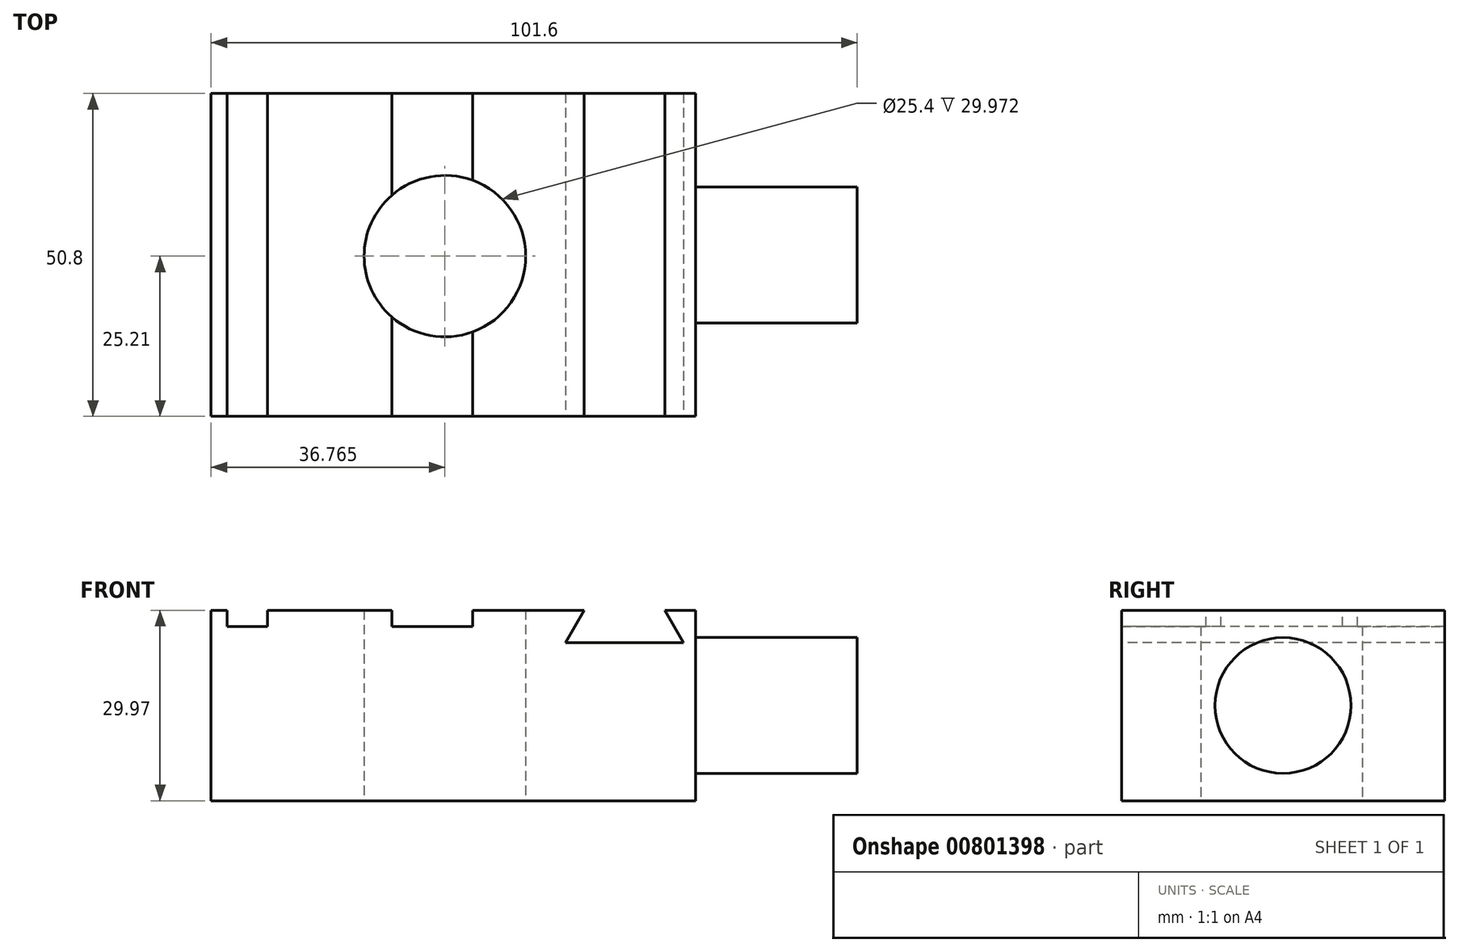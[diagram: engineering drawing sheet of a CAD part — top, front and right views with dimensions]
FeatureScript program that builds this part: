
annotation { "Feature Type Name" : "Feature", "Feature Type Description" : "" }
export const myFeature = defineFeature(function(context is Context, id is Id, definition is map)
    precondition{}
    {
        {
            var Q0;
            Q0=qCreatedBy(makeId("Top.planeOp"),FACE);
            var sketch = newSketch(context, id + "F0", { "sketchPlane" : qUnion([Q0])});
            skLineSegment(sketch, "E0.bottom", {"start": v(-34.76, 25.6) * mm, "end": v(41.44, 25.6) * mm});
            skLineSegment(sketch, "E0.top", {"start": v(-34.76, -25.2) * mm, "end": v(41.44, -25.2) * mm});
            skLineSegment(sketch, "E0.left", {"start": v(-34.76, 25.6) * mm, "end": v(-34.76, -25.2) * mm});
            skLineSegment(sketch, "E0.right", {"start": v(41.44, 25.6) * mm, "end": v(41.44, -25.2) * mm});
            skCircle(sketch, "E1", {"center": v(2, 0) * mm, "radius": 12.7 * mm});
            skSolve(sketch);
        }
        {
            var Q0;
            Q0=makeQuery(id+"F0.imprint","IMPRINT",FACE,{"disambiguationData":[TD([[makeQuery(id+"F0.imprint","IMPRINT",EDGE,{"derivedFrom":sQuery(id+"F0.wireOp",EDGE,"E0.bottom")}),-1.0]])]});
            extrude(context, id + "F1", {"entities" : qUnion([Q0]), "depth" : 29.97 * mm, "offsetDistance" : 25.4 * mm});
        }
        {
            var Q0;
            Q0=makeQuery(id+"F1.opExtrude","CAP_FACE",FACE,{"disambiguationData":[OSD([sQuery(id+"F0.wireOp",EDGE,"E0.bottom"),sQuery(id+"F0.wireOp",EDGE,"E0.top"),sQuery(id+"F0.wireOp",EDGE,"E0.left"),sQuery(id+"F0.wireOp",EDGE,"E0.right"),sQuery(id+"F0.wireOp",EDGE,"E1")])],"isStart":false});
            var sketch = newSketch(context, id + "F2", { "sketchPlane" : qUnion([Q0])});
            skLineSegment(sketch, "E2.bottom", {"start": v(-32.22, 25.6) * mm, "end": v(-25.87, 25.6) * mm});
            skLineSegment(sketch, "E2.top", {"start": v(-32.22, -25.2) * mm, "end": v(-25.87, -25.2) * mm});
            skLineSegment(sketch, "E2.left", {"start": v(-32.22, 25.6) * mm, "end": v(-32.22, -25.2) * mm});
            skLineSegment(sketch, "E2.right", {"start": v(-25.87, 25.6) * mm, "end": v(-25.87, -25.2) * mm});
            skLineSegment(sketch, "E3", {"start": v(-6.35, 25.6) * mm, "end": v(-6.35, -25.2) * mm});
            skLineSegment(sketch, "E4", {"start": v(-6.35, -25.2) * mm, "end": v(6.35, -25.2) * mm});
            skLineSegment(sketch, "E5", {"start": v(6.35, -25.2) * mm, "end": v(6.35, 25.6) * mm});
            skLineSegment(sketch, "E6", {"start": v(6.35, 25.6) * mm, "end": v(-6.35, 25.6) * mm});
            skPoint(sketch, "E7", {"position": v(0, 0) * mm});
            skLineSegment(sketch, "E8", {"start": v(0, 25.6) * mm, "end": v(0, -25.2) * mm, "construction": true});
            skSolve(sketch);
        }
        {
            var Q0;
            Q0=makeQuery(id+"F2.imprint","IMPRINT",FACE,{"disambiguationData":[TD([[makeQuery(id+"F2.imprint","IMPRINT",EDGE,{"derivedFrom":sQuery(id+"F2.wireOp",EDGE,"E2.bottom")}),-1.0]])]});
            var Q1;
            {var subQ0=sQuery(id+"F2.wireOp",EDGE,"E6");Q1=makeQuery(id+"F2.imprint","IMPRINT",FACE,{"disambiguationData":[TD([[makeQuery(id+"F2.imprint","IMPRINT",EDGE,{"derivedFrom":subQ0}),-1.0]])]});}
            var Q2;
            {var subQ0=sQuery(id+"F2.wireOp",EDGE,"E4");Q2=makeQuery(id+"F2.imprint","IMPRINT",FACE,{"disambiguationData":[TD([[makeQuery(id+"F2.imprint","IMPRINT",EDGE,{"derivedFrom":subQ0}),1.0]])]});}
            extrude(context, id + "F3", {"entities" : qUnion([Q0, Q1, Q2]), "operationType" : NewBodyOperationType.REMOVE, "oppositeDirection" : true, "depth" : 2.54 * mm, "offsetDistance" : 25.4 * mm});
        }
        {
            var Q0;
            Q0=makeQuery(id+"F1.opExtrude","SWEPT_FACE",FACE,{"disambiguationData":[OSD([sQuery(id+"F0.wireOp",EDGE,"E0.top")])]});
            var sketch = newSketch(context, id + "F4", { "sketchPlane" : qUnion([Q0])});
            skLineSegment(sketch, "E9", {"start": v(23.9, 29.97) * mm, "end": v(20.96, 24.9) * mm});
            skLineSegment(sketch, "E10", {"start": v(20.96, 24.9) * mm, "end": v(39.53, 24.9) * mm});
            skLineSegment(sketch, "E11", {"start": v(39.53, 24.9) * mm, "end": v(36.6, 29.97) * mm});
            skLineSegment(sketch, "E12", {"start": v(36.6, 29.97) * mm, "end": v(23.9, 29.97) * mm});
            skPoint(sketch, "E13", {"position": v(30.25, 24.9) * mm});
            skLineSegment(sketch, "E14", {"start": v(30.25, 24.9) * mm, "end": v(30.25, 29.97) * mm, "construction": true});
            skSolve(sketch);
        }
        {
            var Q0;
            Q0=makeQuery(id+"F1.opExtrude","SWEPT_FACE",FACE,{"disambiguationData":[OSD([sQuery(id+"F0.wireOp",EDGE,"E0.right")])]});
            var sketch = newSketch(context, id + "F5", { "sketchPlane" : qUnion([Q0])});
            skCircle(sketch, "E15", {"center": v(0.2, 14.99) * mm, "radius": 10.69 * mm});
            skPoint(sketch, "E15.centerSnap0", {"position": v(-25.2, 14.99) * mm});
            skPoint(sketch, "E15.centerSnap1", {"position": v(0.2, 29.97) * mm});
            skSolve(sketch);
        }
        {
            var Q0;
            Q0 = qSketchRegion(id + "F5", true);
            extrude(context, id + "F6", {"entities" : qUnion([Q0]), "operationType" : NewBodyOperationType.ADD, "depth" : 25.4 * mm, "offsetDistance" : 25.4 * mm});
        }
        {
            var Q0;
            Q0=makeQuery(id+"F4.imprint","IMPRINT",FACE,{"disambiguationData":[TD([[makeQuery(id+"F4.imprint","IMPRINT",EDGE,{"derivedFrom":sQuery(id+"F4.wireOp",EDGE,"E9")}),1.0]])]});
            extrude(context, id + "F7", {"entities" : qUnion([Q0]), "operationType" : NewBodyOperationType.REMOVE, "endBound" : BoundingType.THROUGH_ALL, "oppositeDirection" : true, "depth" : 25.4 * mm, "offsetDistance" : 25.4 * mm});
        }
    });
